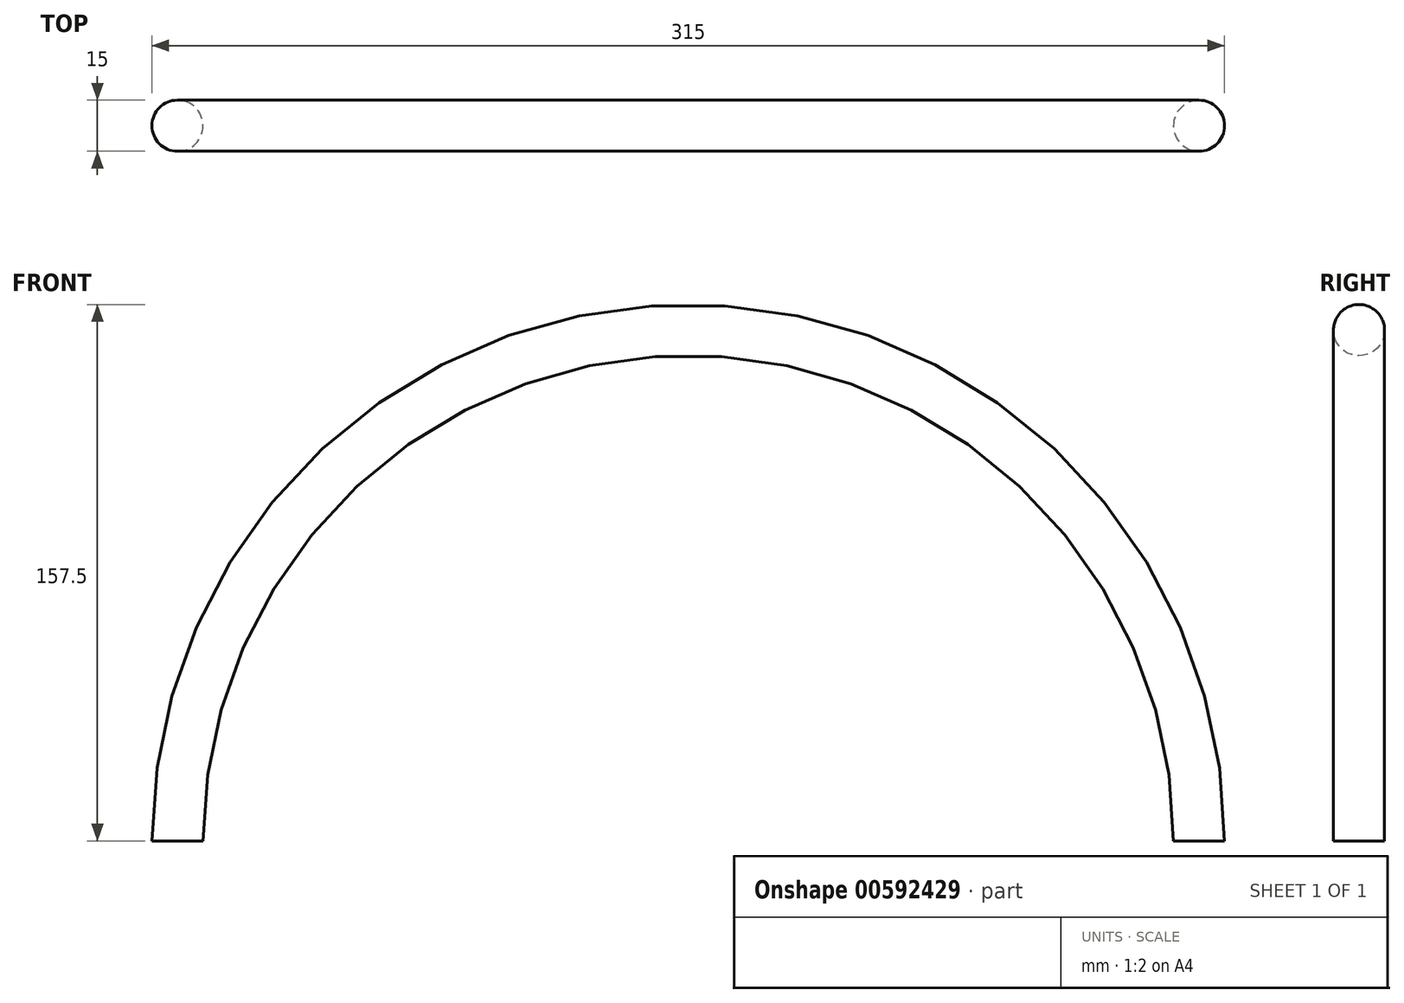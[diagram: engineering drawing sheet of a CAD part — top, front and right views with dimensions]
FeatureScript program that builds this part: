
annotation { "Feature Type Name" : "Feature", "Feature Type Description" : "" }
export const myFeature = defineFeature(function(context is Context, id is Id, definition is map)
    precondition{}
    {
        {
            var Q0;
            Q0=qCreatedBy(makeId("Top.planeOp"),FACE);
            var sketch = newSketch(context, id + "F0", { "sketchPlane" : qUnion([Q0])});
            skCircle(sketch, "E0", {"center": v(150, 0) * mm, "radius": 7.5 * mm});
            skLineSegment(sketch, "E1", {"start": v(0, 0) * mm, "end": v(0, 15.16) * mm});
            skSolve(sketch);
        }
        {
            var Q0;
            Q0=sQuery(id+"F0.wireOp",EDGE,"E0");
            var Q1;
            Q1=sQuery(id+"F0.wireOp",EDGE,"E1");
            revolve(context, id + "F1", {"bodyType" : ToolBodyType.SURFACE, "surfaceEntities" : qUnion([Q0]), "axis" : qUnion([Q1]), "revolveType" : RevolveType.TWO_DIRECTIONS, "angle" : 0 * degree, "angleBack" : 180 * degree});
        }
    });
